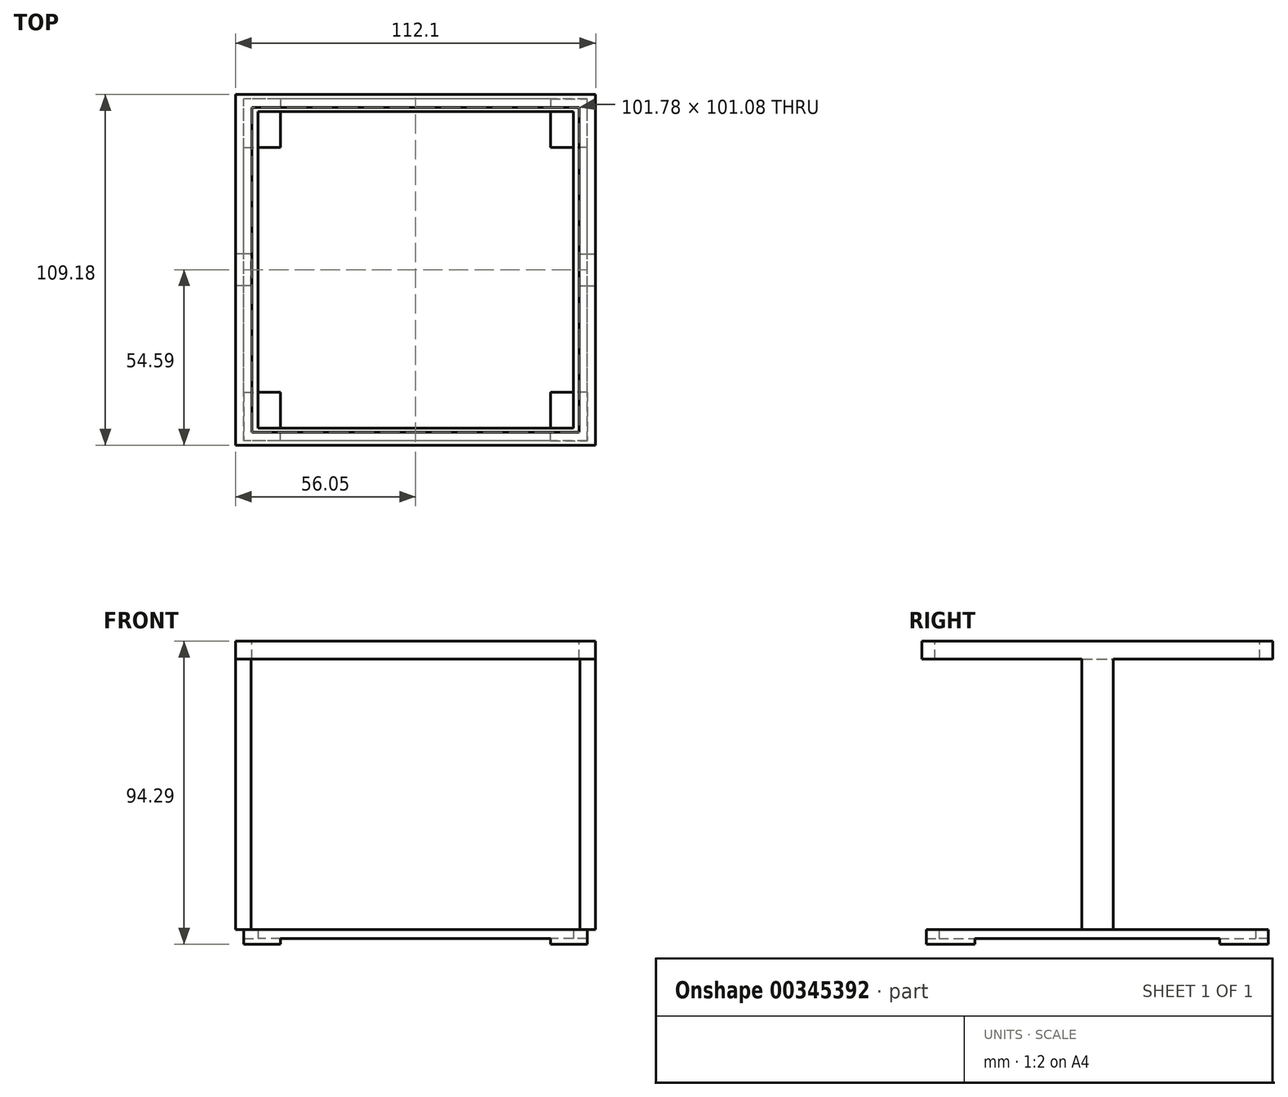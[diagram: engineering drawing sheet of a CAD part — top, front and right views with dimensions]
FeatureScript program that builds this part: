
annotation { "Feature Type Name" : "Feature", "Feature Type Description" : "" }
export const myFeature = defineFeature(function(context is Context, id is Id, definition is map)
    precondition{}
    {
        {
            var Q0;
            Q0=qCreatedBy(makeId("Top.planeOp"),FACE);
            var sketch = newSketch(context, id + "F0", { "sketchPlane" : qUnion([Q0])});
            skLineSegment(sketch, "E0.bottom", {"start": v(56.05, -54.6) * mm, "end": v(-56.05, -54.6) * mm});
            skLineSegment(sketch, "E0.top", {"start": v(56.05, 54.6) * mm, "end": v(-56.05, 54.6) * mm});
            skLineSegment(sketch, "E0.left", {"start": v(56.05, -54.6) * mm, "end": v(56.05, 54.6) * mm});
            skLineSegment(sketch, "E0.right", {"start": v(-56.05, -54.6) * mm, "end": v(-56.05, 54.6) * mm});
            skPoint(sketch, "E0.middle", {"position": v(0, 0) * mm});
            skSolve(sketch);
        }
        {
            var Q0;
            Q0 = qSketchRegion(id + "F0", true);
            extrude(context, id + "F1", {"entities" : qUnion([Q0]), "depth" : 5.6 * mm});
        }
        {
            var Q0;
            Q0=makeQuery(id+"F1.opExtrude","CAP_FACE",FACE,{"disambiguationData":[OSD([sQuery(id+"F0.wireOp",EDGE,"E0.bottom"),sQuery(id+"F0.wireOp",EDGE,"E0.top"),sQuery(id+"F0.wireOp",EDGE,"E0.left"),sQuery(id+"F0.wireOp",EDGE,"E0.right")])],"isStart":false});
            var sketch = newSketch(context, id + "F2", { "sketchPlane" : qUnion([Q0])});
            skLineSegment(sketch, "E1.bottom", {"start": v(50.89, -50.54) * mm, "end": v(-50.89, -50.54) * mm});
            skLineSegment(sketch, "E1.top", {"start": v(50.89, 50.54) * mm, "end": v(-50.89, 50.54) * mm});
            skLineSegment(sketch, "E1.left", {"start": v(50.89, -50.54) * mm, "end": v(50.89, 50.54) * mm});
            skLineSegment(sketch, "E1.right", {"start": v(-50.89, -50.54) * mm, "end": v(-50.89, 50.54) * mm});
            skPoint(sketch, "E1.middle", {"position": v(0, 0) * mm});
            skSolve(sketch);
        }
        {
            var Q0;
            Q0=makeQuery(id+"F2.imprint","IMPRINT",FACE,{"disambiguationData":[TD([[makeQuery(id+"F2.imprint","IMPRINT",EDGE,{"derivedFrom":sQuery(id+"F2.wireOp",EDGE,"E1.bottom")}),-1.0]])]});
            extrude(context, id + "F3", {"entities" : qUnion([Q0]), "operationType" : NewBodyOperationType.REMOVE, "oppositeDirection" : true, "depth" : 25.4 * mm});
        }
        {
            var Q0;
            Q0=makeQuery(id+"F1.opExtrude","SWEPT_FACE",FACE,{"disambiguationData":[OSD([sQuery(id+"F0.wireOp",EDGE,"E0.left")])]});
            var sketch = newSketch(context, id + "F4", { "sketchPlane" : qUnion([Q0])});
            skLineSegment(sketch, "E2.bottom", {"start": v(0, 5.59) * mm, "end": v(4.9, 5.59) * mm});
            skLineSegment(sketch, "E2.top", {"start": v(0, -84.13) * mm, "end": v(4.9, -84.13) * mm});
            skLineSegment(sketch, "E2.left", {"start": v(0, 5.59) * mm, "end": v(0, -84.13) * mm});
            skLineSegment(sketch, "E2.right", {"start": v(4.9, 5.59) * mm, "end": v(4.9, -84.13) * mm});
            skSolve(sketch);
        }
        {
            var Q0;
            {var subQ0=sQuery(id+"F4.wireOp",EDGE,"E2.top");Q0=makeQuery(id+"F4.imprint","IMPRINT",FACE,{"disambiguationData":[TD([[makeQuery(id+"F4.imprint","IMPRINT",EDGE,{"derivedFrom":subQ0}),1.0]])]});}
            extrude(context, id + "F5", {"entities" : qUnion([Q0]), "operationType" : NewBodyOperationType.ADD, "oppositeDirection" : true, "depth" : 4.83 * mm});
        }
        {
            var Q0;
            Q0=makeQuery(id+"F1.opExtrude","SWEPT_BODY",BODY,{"disambiguationData":[OSD([sQuery(id+"F0.wireOp",EDGE,"E0.bottom"),sQuery(id+"F0.wireOp",EDGE,"E0.top"),sQuery(id+"F0.wireOp",EDGE,"E0.left"),sQuery(id+"F0.wireOp",EDGE,"E0.right")])]});
            var Q1;
            Q1=qCreatedBy(makeId("Right.planeOp"),FACE);
            mirror(context, id + "F6", {"operationType" : NewBodyOperationType.ADD, "entities" : qUnion([Q0]), "mirrorPlane" : qUnion([Q1])});
        }
        {
            var Q0;
            Q0=makeQuery(id+"F5.opExtrude","SWEPT_FACE",FACE,{"disambiguationData":[OSD([sQuery(id+"F4.wireOp",EDGE,"E2.top")])]});
            var sketch = newSketch(context, id + "F7", { "sketchPlane" : qUnion([Q0])});
            skLineSegment(sketch, "E3.bottom", {"start": v(53.43, 53.24) * mm, "end": v(-53.43, 53.24) * mm});
            skLineSegment(sketch, "E3.top", {"start": v(53.43, -53.24) * mm, "end": v(-53.43, -53.24) * mm});
            skLineSegment(sketch, "E3.left", {"start": v(53.43, 53.24) * mm, "end": v(53.43, -53.24) * mm});
            skLineSegment(sketch, "E3.right", {"start": v(-53.43, 53.24) * mm, "end": v(-53.43, -53.24) * mm});
            skPoint(sketch, "E3.middle", {"position": v(0, 0) * mm});
            skSolve(sketch);
        }
        {
            var Q0;
            Q0 = qSketchRegion(id + "F7", true);
            extrude(context, id + "F8", {"entities" : qUnion([Q0]), "operationType" : NewBodyOperationType.ADD, "depth" : 2.8 * mm});
        }
        {
            var Q0;
            Q0=makeQuery(id+"F8.opExtrude","CAP_FACE",FACE,{"disambiguationData":[OSD([sQuery(id+"F7.wireOp",EDGE,"E3.bottom"),sQuery(id+"F7.wireOp",EDGE,"E3.top"),sQuery(id+"F7.wireOp",EDGE,"E3.left"),sQuery(id+"F7.wireOp",EDGE,"E3.right")])],"isStart":false});
            var sketch = newSketch(context, id + "F9", { "sketchPlane" : qUnion([Q0])});
            skLineSegment(sketch, "E4.bottom", {"start": v(49.07, 49.3) * mm, "end": v(-49.07, 49.3) * mm});
            skLineSegment(sketch, "E4.top", {"start": v(49.07, -49.3) * mm, "end": v(-49.07, -49.3) * mm});
            skLineSegment(sketch, "E4.left", {"start": v(49.07, 49.3) * mm, "end": v(49.07, -49.3) * mm});
            skLineSegment(sketch, "E4.right", {"start": v(-49.07, 49.3) * mm, "end": v(-49.07, -49.3) * mm});
            skPoint(sketch, "E4.middle", {"position": v(0, 0) * mm});
            skSolve(sketch);
        }
        {
            var Q0;
            Q0=makeQuery(id+"F9.imprint","IMPRINT",FACE,{"disambiguationData":[TD([[makeQuery(id+"F9.imprint","IMPRINT",EDGE,{"derivedFrom":sQuery(id+"F9.wireOp",EDGE,"E4.bottom")}),1.0]])]});
            extrude(context, id + "F10", {"entities" : qUnion([Q0]), "operationType" : NewBodyOperationType.REMOVE, "oppositeDirection" : true, "depth" : 25.4 * mm});
        }
        {
            var Q0;
            Q0=makeQuery(id+"F8.opExtrude","CAP_FACE",FACE,{"disambiguationData":[OSD([sQuery(id+"F7.wireOp",EDGE,"E3.bottom"),sQuery(id+"F7.wireOp",EDGE,"E3.top"),sQuery(id+"F7.wireOp",EDGE,"E3.left"),sQuery(id+"F7.wireOp",EDGE,"E3.right")])],"isStart":false});
            var sketch = newSketch(context, id + "F11", { "sketchPlane" : qUnion([Q0])});
            skLineSegment(sketch, "E5.bottom", {"start": v(-53.43, -53.24) * mm, "end": v(-42, -53.24) * mm});
            skLineSegment(sketch, "E5.top", {"start": v(-53.43, -38.05) * mm, "end": v(-42, -38.05) * mm});
            skLineSegment(sketch, "E5.left", {"start": v(-53.43, -53.24) * mm, "end": v(-53.43, -38.05) * mm});
            skLineSegment(sketch, "E5.right", {"start": v(-42, -53.24) * mm, "end": v(-42, -38.05) * mm});
            skSolve(sketch);
        }
        {
            var Q0;
            {var subQ1=sQuery(id+"F11.wireOp",EDGE,"E5.bottom");Q0=makeQuery(id+"F11.imprint","IMPRINT",FACE,{"disambiguationData":[TD([[makeQuery(id+"F11.imprint","IMPRINT",EDGE,{"derivedFrom":subQ1}),-1.0]])]});}
            var Q1;
            {var subQ0=sQuery(id+"F11.wireOp",EDGE,"E5.right");var subQ1=sQuery(id+"F11.wireOp",EDGE,"E5.top");var subQ2=makeQuery(id+"F11.imprint","INTERSECT",VERTEX,{"derivedFrom":[subQ1,subQ0]});Q1=makeQuery(id+"F11.imprint","IMPRINT",FACE,{"disambiguationData":[TD([[makeQuery(id+"F11.imprint","IMPRINT",EDGE,{"disambiguationData":[TD([[subQ2,1.0]])],"derivedFrom":subQ1}),-1.0]])]});}
            extrude(context, id + "F12", {"entities" : qUnion([Q0, Q1]), "operationType" : NewBodyOperationType.ADD, "depth" : 1.78 * mm});
        }
        {
            var Q0;
            Q0=makeQuery(id+"F1.opExtrude","SWEPT_BODY",BODY,{"disambiguationData":[OSD([sQuery(id+"F0.wireOp",EDGE,"E0.bottom"),sQuery(id+"F0.wireOp",EDGE,"E0.top"),sQuery(id+"F0.wireOp",EDGE,"E0.left"),sQuery(id+"F0.wireOp",EDGE,"E0.right")])]});
            var Q1;
            Q1=qCreatedBy(makeId("Front.planeOp"),FACE);
            mirror(context, id + "F13", {"operationType" : NewBodyOperationType.ADD, "entities" : qUnion([Q0]), "mirrorPlane" : qUnion([Q1])});
        }
        {
            var Q0;
            Q0=makeQuery(id+"F1.opExtrude","SWEPT_BODY",BODY,{"disambiguationData":[OSD([sQuery(id+"F0.wireOp",EDGE,"E0.bottom"),sQuery(id+"F0.wireOp",EDGE,"E0.top"),sQuery(id+"F0.wireOp",EDGE,"E0.left"),sQuery(id+"F0.wireOp",EDGE,"E0.right")])]});
            var Q1;
            Q1=qCreatedBy(makeId("Right.planeOp"),FACE);
            mirror(context, id + "F14", {"operationType" : NewBodyOperationType.ADD, "entities" : qUnion([Q0]), "mirrorPlane" : qUnion([Q1])});
        }
        {
            var Q0;
            Q0=makeQuery(id+"F1.opExtrude","CAP_FACE",FACE,{"disambiguationData":[OSD([sQuery(id+"F0.wireOp",EDGE,"E0.bottom"),sQuery(id+"F0.wireOp",EDGE,"E0.top"),sQuery(id+"F0.wireOp",EDGE,"E0.left"),sQuery(id+"F0.wireOp",EDGE,"E0.right")])],"isStart":false});
            var sketch = newSketch(context, id + "F15", { "sketchPlane" : qUnion([Q0])});
            skSolve(sketch);
        }
        {
            var Q0;
            Q0 = qSketchRegion(id + "F15", true);
            var Q1;
            Q1=makeQuery(id+"F15.imprint","IMPRINT",FACE,{"disambiguationData":[TD([[makeQuery(id+"F15.imprint","IMPRINT",EDGE,{"derivedFrom":makeQuery(id+"F1.opExtrude","CAP_EDGE",EDGE,{"disambiguationData":[OSD([sQuery(id+"F0.wireOp",EDGE,"E0.bottom")])],"isStart":false})}),-1.0]])]});
            extrude(context, id + "F16", {"entities" : qUnion([Q0, Q1]), "operationType" : NewBodyOperationType.ADD, "oppositeDirection" : true, "depth" : 1.02 * mm, "offsetDistance" : 25.4 * mm});
        }
    });
